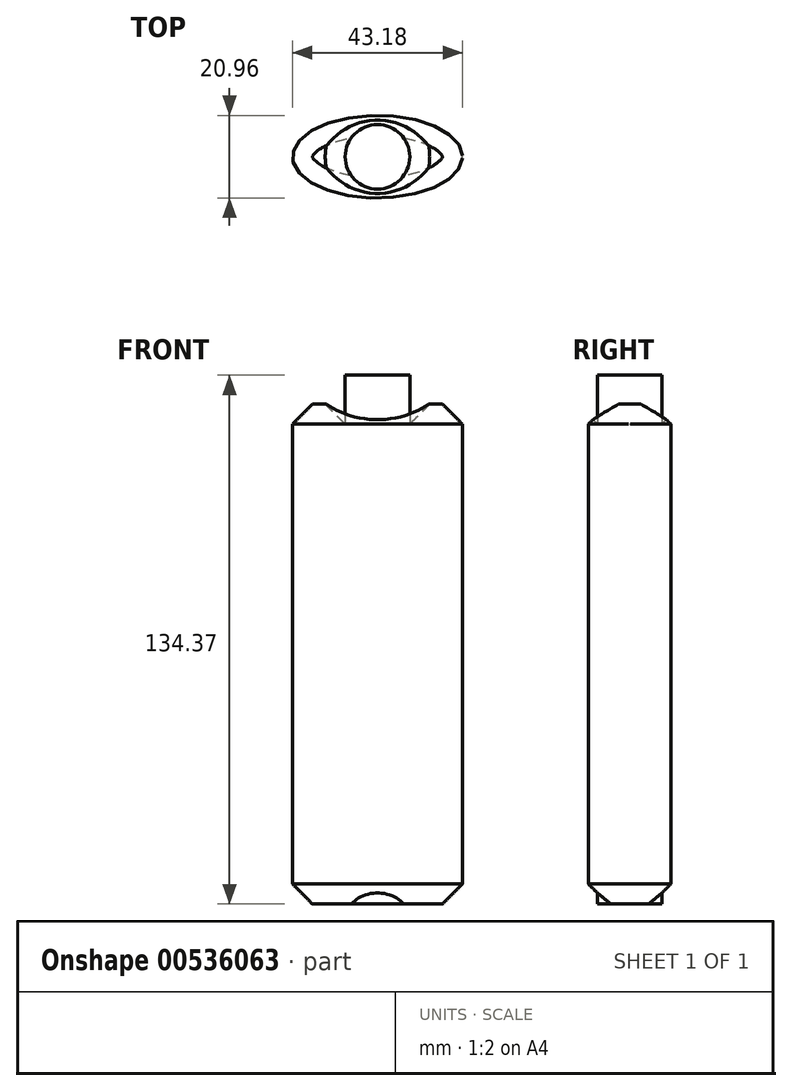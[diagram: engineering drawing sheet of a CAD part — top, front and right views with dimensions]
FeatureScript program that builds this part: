
annotation { "Feature Type Name" : "Feature", "Feature Type Description" : "" }
export const myFeature = defineFeature(function(context is Context, id is Id, definition is map)
    precondition{}
    {
        {
            var Q0;
            Q0=qCreatedBy(makeId("Top.planeOp"),FACE);
            var sketch = newSketch(context, id + "F0", { "sketchPlane" : qUnion([Q0])});
            skEllipse(sketch, "E0", {"center": v(0, 0) * mm, "majorRadius": 21.6 * mm, "minorRadius": 10.48 * mm, "majorAxis": v(1, 0)});
            skCircle(sketch, "E1", {"center": v(0, 0) * mm, "radius": 8.2 * mm});
            skSolve(sketch);
        }
        {
            var Q0;
            Q0=makeQuery(id+"F0.imprint","IMPRINT",FACE,{"disambiguationData":[TD([[makeQuery(id+"F0.imprint","IMPRINT",EDGE,{"derivedFrom":sQuery(id+"F0.wireOp",EDGE,"E0")}),1.0]])]});
            extrude(context, id + "F1", {"entities" : qUnion([Q0]), "depth" : 127 * mm, "offsetDistance" : 25.4 * mm});
        }
        {
            var Q0;
            Q0=makeQuery(id+"F1.opExtrude","CAP_FACE",FACE,{"disambiguationData":[OSD([sQuery(id+"F0.wireOp",EDGE,"E0")])],"isStart":false});
            var Q1;
            Q1=makeQuery(id+"F1.opExtrude","SWEPT_FACE",FACE,{"disambiguationData":[OSD([sQuery(id+"F0.wireOp",EDGE,"E0")])]});
            chamfer(context, id + "F2", {"entities" : qUnion([Q0, Q1]), "width" : 5.08 * mm, "tangentPropagation" : true});
        }
        {
            var Q0;
            Q0=makeQuery(id+"F0.imprint","IMPRINT",FACE,{"disambiguationData":[TD([[makeQuery(id+"F0.imprint","IMPRINT",EDGE,{"derivedFrom":sQuery(id+"F0.wireOp",EDGE,"E1")}),1.0]])]});
            extrude(context, id + "F3", {"entities" : qUnion([Q0]), "operationType" : NewBodyOperationType.ADD, "depth" : 134.37 * mm, "offsetDistance" : 25.4 * mm});
        }
    });
